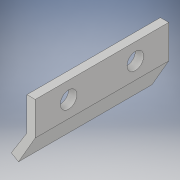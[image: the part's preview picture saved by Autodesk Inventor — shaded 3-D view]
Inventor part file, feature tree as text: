
AUTODESK INVENTOR PART (.ipt)
format: ipt  version: 2017 (Build 210142000, 142)  size: 109,568 bytes
history: native  units: in
note: dims shown in document units (in); Inventor stores cm internally (conversion verified against a paired STEP export)
features: sketch x2, extrude x1, hole x1
ambient origin geometry x8: Origin, YZ Plane, XZ Plane, XY Plane, X Axis, Y Axis, Z Axis, Center Point
bodies: Solid1 (feature_tree)
feature tree (4):
  extrude  "Extrusion1"  TaperAngle=120.0deg  [1 undecoded]
  hole  "Hole1"  [1 undecoded]
  sketch  "Sketch2"  dims[d0=0.25in d1=120.0deg]
  sketch  "Sketch3"  dims[d2=0.25in d3=0.0625in d4=0.0625in d5=1.0in d6=0.0in d7=0.25in d8=0.125in d9=0.125in d10=0.75in d11=0.375in d12=0.25in d13=0.5635in d14=1.0in d15=0.8108in]
note: 2 required parameter values undecoded (feature->parameter linkage not recoverable at this tier; creation-order binding heuristic only, values carry confidence <= 0.55)
